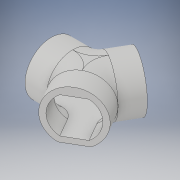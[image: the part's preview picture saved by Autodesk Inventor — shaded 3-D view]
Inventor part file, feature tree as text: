
AUTODESK INVENTOR PART (.ipt)
format: ipt  version: 2017 (Build 210142000, 142)  size: 245,248 bytes
history: native  units: in
note: dims shown in document units (in); Inventor stores cm internally (conversion verified against a paired STEP export)
features: sketch x4, extrude x2, other x2, pattern_circular x2, sweep x1, mirror x1
ambient origin geometry x8: Origin, YZ Plane, XZ Plane, XY Plane, X Axis, Y Axis, Z Axis, Center Point
bodies: Solid1 (feature_tree)
feature tree (12):
  extrude  "corridor"  Depth=9.7746in
  other  "found rotaion axis"
  other  "rotaion axis"
  pattern_circular  "other corridors"  Count=3 Angle=360.0deg
  sweep  "curve edjes"
  pattern_circular  "repeat curve edjes"  [2 undecoded]
  extrude  "bottom hole fill up"  [1 undecoded]
  mirror  "top hole fill up"
  sketch  "Sketch1"  dims[d10=6.6667in d11=4.0in d12=4.0in d13=0.0in d14=9.7746in]
  sketch  "Sketch4"  dims[d15=2.8217in d16=1.1811in d17=360.0deg]
  sketch  "Sketch5"  dims[d24=0.0in d25=0.0in d26=1.1811in d27=360.0deg]
  sketch  "Sketch7"  dims[d37=1.554in d38=0.0in d46=1.0in]
note: 3 required parameter values undecoded (feature->parameter linkage not recoverable at this tier; creation-order binding heuristic only, values carry confidence <= 0.55)
